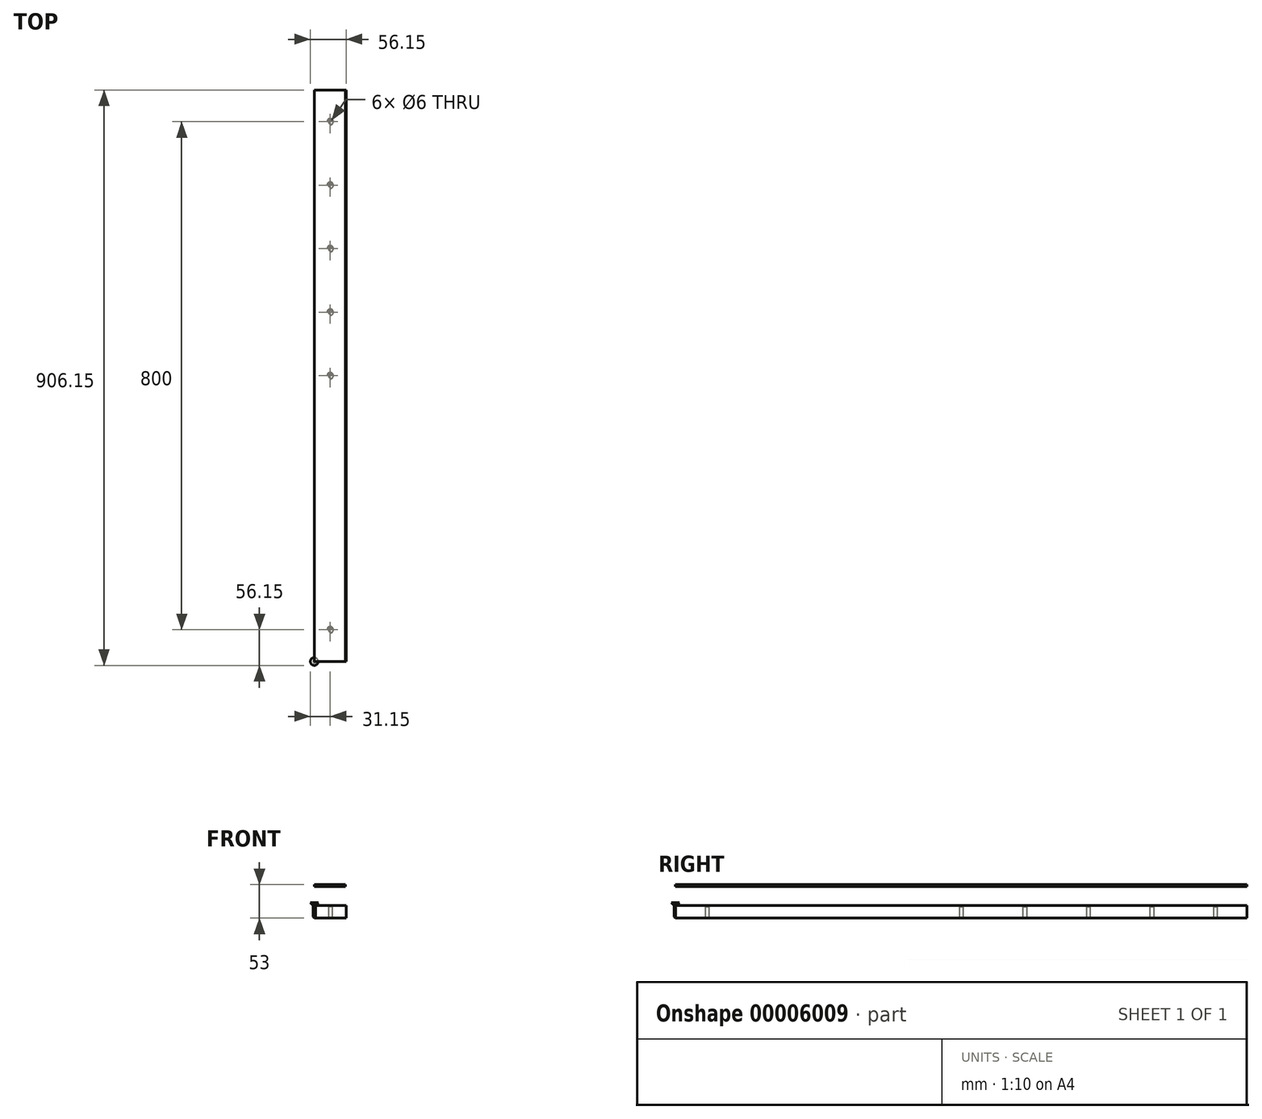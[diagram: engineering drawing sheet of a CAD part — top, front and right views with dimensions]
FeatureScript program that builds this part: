
annotation { "Feature Type Name" : "Feature", "Feature Type Description" : "" }
export const myFeature = defineFeature(function(context is Context, id is Id, definition is map)
    precondition{}
    {
        {
            var Q0;
            Q0=qCreatedBy(makeId("Top.planeOp"),FACE);
            var sketch = newSketch(context, id + "F0", { "sketchPlane" : qUnion([Q0])});
            skLineSegment(sketch, "E0.bottom", {"start": v(0, 0) * mm, "end": v(50, 0) * mm});
            skLineSegment(sketch, "E0.top", {"start": v(0, 900) * mm, "end": v(50, 900) * mm});
            skLineSegment(sketch, "E0.left", {"start": v(0, 0) * mm, "end": v(0, 900) * mm});
            skLineSegment(sketch, "E0.right", {"start": v(50, 0) * mm, "end": v(50, 900) * mm});
            skLineSegment(sketch, "E1", {"start": v(25, 900) * mm, "end": v(25, 850) * mm, "construction": true});
            skLineSegment(sketch, "E2", {"start": v(25, 850) * mm, "end": v(25, 750) * mm, "construction": true});
            skLineSegment(sketch, "E3", {"start": v(25, 750) * mm, "end": v(25, 650) * mm, "construction": true});
            skLineSegment(sketch, "E4", {"start": v(25, 650) * mm, "end": v(25, 0) * mm, "construction": true});
            skPoint(sketch, "E5", {"position": v(25, 50) * mm});
            skPoint(sketch, "E6", {"position": v(25, 550) * mm});
            skPoint(sketch, "E7", {"position": v(25, 450) * mm});
            skCircle(sketch, "E8", {"center": v(25, 850) * mm, "radius": 3 * mm});
            skCircle(sketch, "E9", {"center": v(25, 750) * mm, "radius": 3 * mm});
            skCircle(sketch, "E10", {"center": v(25, 650) * mm, "radius": 3 * mm});
            skCircle(sketch, "E11", {"center": v(25, 550) * mm, "radius": 3 * mm});
            skCircle(sketch, "E12", {"center": v(25, 450) * mm, "radius": 3 * mm});
            skCircle(sketch, "E13", {"center": v(25, 50) * mm, "radius": 3 * mm});
            skSolve(sketch);
        }
        {
            var Q0;
            Q0 = qSketchRegion(id + "F0", true);
            extrude(context, id + "F1", {"entities" : qUnion([Q0]), "depth" : 20 * mm});
        }
        {
            var Q0;
            Q0=makeQuery(id+"F1.opExtrude","CAP_EDGE",EDGE,{"disambiguationData":[OSD([sQuery(id+"F0.wireOp",EDGE,"E8")])],"isStart":false});
            var Q1;
            Q1=makeQuery(id+"F1.opExtrude","CAP_EDGE",EDGE,{"disambiguationData":[OSD([sQuery(id+"F0.wireOp",EDGE,"E9")])],"isStart":false});
            var Q2;
            Q2=makeQuery(id+"F1.opExtrude","CAP_EDGE",EDGE,{"disambiguationData":[OSD([sQuery(id+"F0.wireOp",EDGE,"E10")])],"isStart":false});
            var Q3;
            Q3=makeQuery(id+"F1.opExtrude","CAP_EDGE",EDGE,{"disambiguationData":[OSD([sQuery(id+"F0.wireOp",EDGE,"E11")])],"isStart":false});
            var Q4;
            Q4=makeQuery(id+"F1.opExtrude","CAP_EDGE",EDGE,{"disambiguationData":[OSD([sQuery(id+"F0.wireOp",EDGE,"E12")])],"isStart":false});
            var Q5;
            Q5=makeQuery(id+"F1.opExtrude","CAP_EDGE",EDGE,{"disambiguationData":[OSD([sQuery(id+"F0.wireOp",EDGE,"E13")])],"isStart":false});
            chamfer(context, id + "F2", {"entities" : qUnion([Q0, Q1, Q2, Q3, Q4, Q5]), "chamferType" : ChamferType.OFFSET_ANGLE, "width" : 2 * mm, "oppositeDirection" : false, "angle" : 45 * degree, "tangentPropagation" : true});
        }
        {
            var Q0;
            Q0=qCreatedBy(makeId("Top.planeOp"),FACE);
            var sketch = newSketch(context, id + "F3", { "sketchPlane" : qUnion([Q0])});
            skLineSegment(sketch, "E14.bottom", {"start": v(0, 0) * mm, "end": v(49, 0) * mm});
            skLineSegment(sketch, "E14.top", {"start": v(0, 900) * mm, "end": v(49, 900) * mm});
            skLineSegment(sketch, "E14.left", {"start": v(0, 0) * mm, "end": v(0, 900) * mm});
            skLineSegment(sketch, "E14.right", {"start": v(49, 0) * mm, "end": v(49, 900) * mm});
            skSolve(sketch);
        }
        {
            var Q0;
            Q0=makeQuery(id+"F3.imprint","IMPRINT",FACE,{"disambiguationData":[TD([[makeQuery(id+"F3.imprint","IMPRINT",EDGE,{"derivedFrom":sQuery(id+"F3.wireOp",EDGE,"E14.bottom")}),1.0]])]});
            extrude(context, id + "F4", {"entities" : qUnion([Q0]), "depth" : 3 * mm});
        }
        {
            var Q0;
            Q0=makeQuery(id+"F4.opExtrude","SWEPT_BODY",BODY,{"disambiguationData":[OSD([sQuery(id+"F3.wireOp",EDGE,"E14.bottom"),sQuery(id+"F3.wireOp",EDGE,"E14.top"),sQuery(id+"F3.wireOp",EDGE,"E14.left"),sQuery(id+"F3.wireOp",EDGE,"E14.right")])]});
            var Q1;
            Q1=makeQuery(id+"F4.opExtrude","CAP_FACE",FACE,{"disambiguationData":[OSD([sQuery(id+"F3.wireOp",EDGE,"E14.bottom"),sQuery(id+"F3.wireOp",EDGE,"E14.top"),sQuery(id+"F3.wireOp",EDGE,"E14.left"),sQuery(id+"F3.wireOp",EDGE,"E14.right")])],"isStart":false});
            transform(context, id + "F5", {"entities" : qUnion([Q0]), "transformType" : TransformType.TRANSLATION_DISTANCE, "transformDirection" : qUnion([Q1]), "distance" : 50 * mm, "makeCopy" : false});
        }
        {
            var Q0;
            Q0=qCreatedBy(makeId("Right.planeOp"),FACE);
            var sketch = newSketch(context, id + "F6", { "sketchPlane" : qUnion([Q0])});
            skLineSegment(sketch, "E15", {"start": v(0, 0) * mm, "end": v(-2, 2) * mm});
            skLineSegment(sketch, "E16", {"start": v(-2, 2) * mm, "end": v(-2, 20) * mm});
            skLineSegment(sketch, "E17", {"start": v(-2, 20) * mm, "end": v(-6.15, 24.15) * mm});
            skLineSegment(sketch, "E18", {"start": v(-6.15, 24.15) * mm, "end": v(0, 24.15) * mm});
            skLineSegment(sketch, "E19", {"start": v(0, 24.15) * mm, "end": v(0, 0) * mm});
            skSolve(sketch);
        }
        {
            var Q0;
            Q0=makeQuery(id+"F6.imprint","IMPRINT",FACE,{"disambiguationData":[TD([[makeQuery(id+"F6.imprint","IMPRINT",EDGE,{"derivedFrom":sQuery(id+"F6.wireOp",EDGE,"E15")}),-1.0]])]});
            var Q1;
            Q1=sQuery(id+"F6.wireOp",EDGE,"E19");
            revolve(context, id + "F7", {"entities" : qUnion([Q0]), "axis" : qUnion([Q1]), "revolveType" : RevolveType.FULL});
        }
    });
